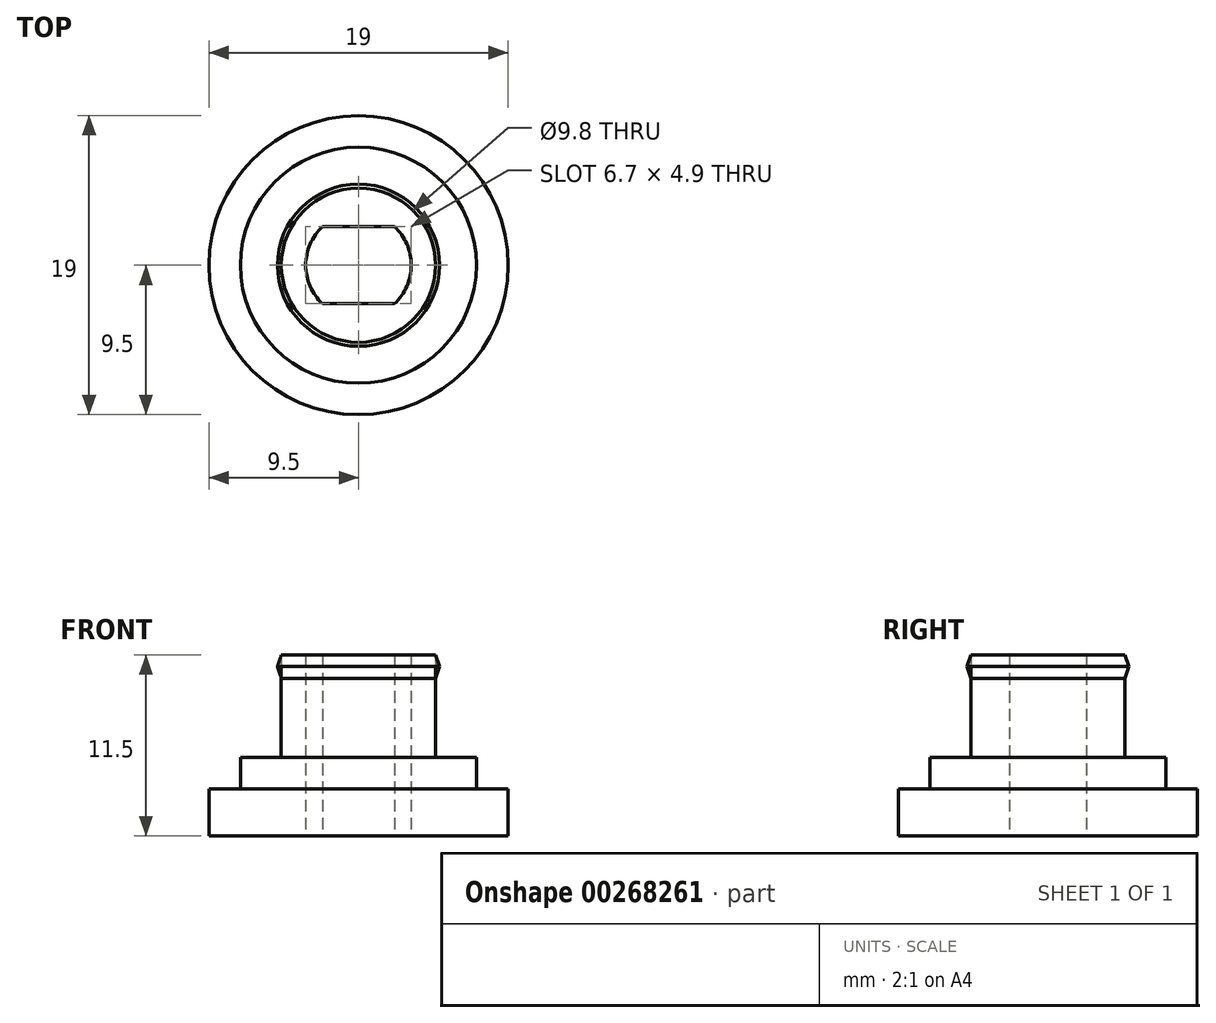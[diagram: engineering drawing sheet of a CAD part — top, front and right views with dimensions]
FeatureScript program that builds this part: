
annotation { "Feature Type Name" : "Feature", "Feature Type Description" : "" }
export const myFeature = defineFeature(function(context is Context, id is Id, definition is map)
    precondition{}
    {
        {
            var Q0;
            Q0=qCreatedBy(makeId("Top.planeOp"),FACE);
            var sketch = newSketch(context, id + "F0", { "sketchPlane" : qUnion([Q0])});
            skCircle(sketch, "E0", {"center": v(0, 0) * mm, "radius": 9.5 * mm});
            skCircle(sketch, "E1", {"center": v(0, 0) * mm, "radius": 7.5 * mm});
            skCircle(sketch, "E2", {"center": v(0, 0) * mm, "radius": 4.9 * mm});
            skArc(sketch, "E3", {"start": v(-2.28, 2.45) * mm, "mid": v(-3.35, 0) * mm, "end": v(-2.28, -2.45) * mm});
            skLineSegment(sketch, "E4.bottom", {"start": v(2.28, -2.45) * mm, "end": v(-2.28, -2.45) * mm});
            skLineSegment(sketch, "E4.top", {"start": v(2.28, 2.45) * mm, "end": v(-2.28, 2.45) * mm});
            skArc(sketch, "E5.trimOffspring", {"start": v(2.28, -2.45) * mm, "mid": v(3.35, 0) * mm, "end": v(2.28, 2.45) * mm});
            skSolve(sketch);
        }
        {
            var Q0;
            Q0 = qSketchRegion(id + "F0", true);
            extrude(context, id + "F1", {"entities" : qUnion([Q0]), "depth" : 3 * mm});
        }
        {
            var Q0;
            Q0=makeQuery(id+"F0.imprint","IMPRINT",FACE,{"disambiguationData":[TD([[makeQuery(id+"F0.imprint","IMPRINT",EDGE,{"derivedFrom":sQuery(id+"F0.wireOp",EDGE,"E1")}),1.0]])]});
            extrude(context, id + "F2", {"entities" : qUnion([Q0]), "operationType" : NewBodyOperationType.ADD, "depth" : 5 * mm});
        }
        {
            var Q0;
            Q0=makeQuery(id+"F0.imprint","IMPRINT",FACE,{"disambiguationData":[TD([[makeQuery(id+"F0.imprint","IMPRINT",EDGE,{"derivedFrom":sQuery(id+"F0.wireOp",EDGE,"E2")}),1.0]])]});
            extrude(context, id + "F3", {"entities" : qUnion([Q0]), "operationType" : NewBodyOperationType.ADD, "depth" : 11.5 * mm});
        }
        {
            var Q0;
            Q0=qCreatedBy(makeId("Front.planeOp"),FACE);
            var sketch = newSketch(context, id + "F4", { "sketchPlane" : qUnion([Q0])});
            skLineSegment(sketch, "E6.bottom", {"start": v(4.9, 11.5) * mm, "end": v(5.15, 11.5) * mm, "construction": true});
            skLineSegment(sketch, "E6.top", {"start": v(4.9, 10) * mm, "end": v(5.15, 10) * mm, "construction": true});
            skLineSegment(sketch, "E6.left", {"start": v(4.9, 11.5) * mm, "end": v(4.9, 10) * mm, "construction": true});
            skLineSegment(sketch, "E6.right", {"start": v(5.15, 11.5) * mm, "end": v(5.15, 10) * mm, "construction": true});
            skPoint(sketch, "E7", {"position": v(5.15, 10.75) * mm});
            skLineSegment(sketch, "E8", {"start": v(4.9, 11.5) * mm, "end": v(5.15, 10.75) * mm});
            skLineSegment(sketch, "E9", {"start": v(5.15, 10.75) * mm, "end": v(4.9, 10) * mm});
            skLineSegment(sketch, "E10", {"start": v(4.9, 11.5) * mm, "end": v(4.9, 10) * mm});
            skLineSegment(sketch, "E11", {"start": v(4.9, 11.5) * mm, "end": v(4.9, 5) * mm});
            skLineSegment(sketch, "E12", {"start": v(-4.9, 5) * mm, "end": v(-4.9, 11.5) * mm});
            skLineSegment(sketch, "E13", {"start": v(0, 0) * mm, "end": v(0, 17.95) * mm});
            skSolve(sketch);
        }
        {
            var Q0;
            Q0 = qSketchRegion(id + "F4", true);
            var Q1;
            Q1=sQuery(id+"F4.wireOp",EDGE,"E13");
            revolve(context, id + "F5", {"entities" : qUnion([Q0]), "axis" : qUnion([Q1]), "revolveType" : RevolveType.FULL});
        }
    });
